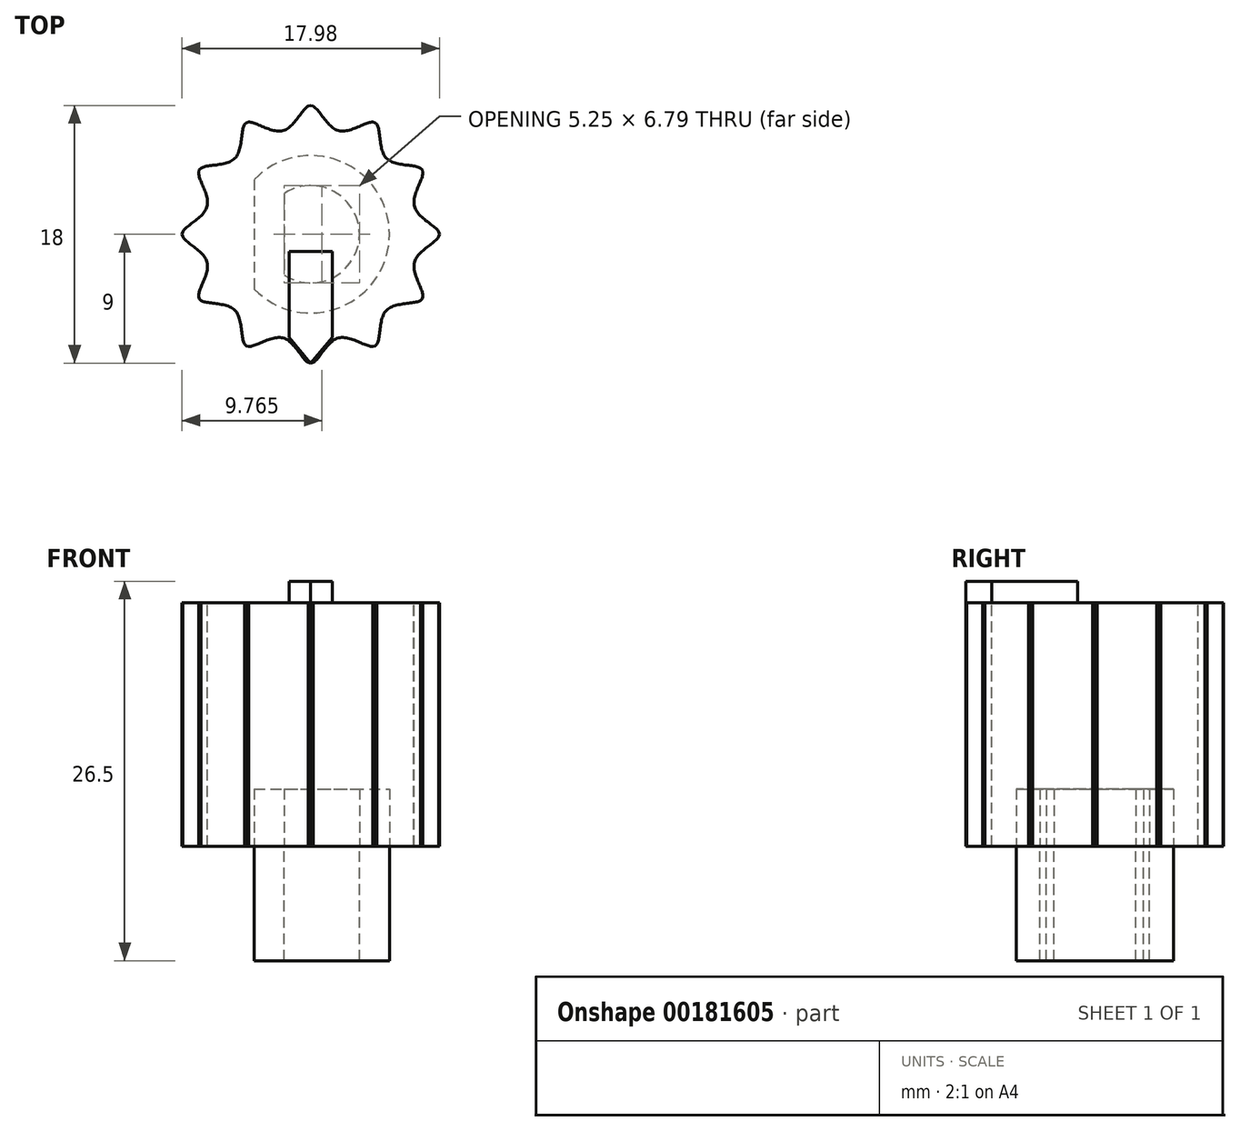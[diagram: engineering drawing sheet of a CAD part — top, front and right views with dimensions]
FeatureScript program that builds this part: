
annotation { "Feature Type Name" : "Feature", "Feature Type Description" : "" }
export const myFeature = defineFeature(function(context is Context, id is Id, definition is map)
    precondition{}
    {
        {
            var Q0;
            Q0=qCreatedBy(makeId("Top.planeOp"),FACE);
            var sketch = newSketch(context, id + "F0", { "sketchPlane" : qUnion([Q0])});
            skCircle(sketch, "E0", {"center": v(0, 0) * mm, "radius": 5.5 * mm});
            skLineSegment(sketch, "E1", {"start": v(-3.95, 3.83) * mm, "end": v(-3.95, -3.83) * mm});
            skArc(sketch, "E2", {"start": v(-1.85, 2.85) * mm, "mid": v(3.4, 0) * mm, "end": v(-1.85, -2.85) * mm});
            skLineSegment(sketch, "E3", {"start": v(-1.85, 2.85) * mm, "end": v(-1.85, -2.85) * mm});
            skLineSegment(sketch, "E4.0", {"start": v(-7.8, -4.5) * mm, "end": v(-9, 0) * mm});
            skLineSegment(sketch, "E4.1", {"start": v(-9, 0) * mm, "end": v(-7.8, 4.5) * mm});
            skLineSegment(sketch, "E4.2", {"start": v(-7.8, 4.5) * mm, "end": v(-4.5, 7.8) * mm});
            skLineSegment(sketch, "E4.3", {"start": v(-4.5, 7.8) * mm, "end": v(0, 9) * mm});
            skLineSegment(sketch, "E4.4", {"start": v(0, 9) * mm, "end": v(4.5, 7.8) * mm});
            skLineSegment(sketch, "E4.5", {"start": v(4.5, 7.8) * mm, "end": v(7.8, 4.5) * mm});
            skLineSegment(sketch, "E4.6", {"start": v(7.8, 4.5) * mm, "end": v(9, 0) * mm});
            skLineSegment(sketch, "E4.7", {"start": v(9, 0) * mm, "end": v(7.8, -4.5) * mm});
            skLineSegment(sketch, "E4.8", {"start": v(7.8, -4.5) * mm, "end": v(4.5, -7.8) * mm});
            skLineSegment(sketch, "E4.9", {"start": v(4.5, -7.8) * mm, "end": v(0, -9) * mm});
            skLineSegment(sketch, "E4.10", {"start": v(0, -9) * mm, "end": v(-4.5, -7.8) * mm});
            skLineSegment(sketch, "E4.11", {"start": v(-4.5, -7.8) * mm, "end": v(-7.8, -4.5) * mm});
            skLineSegment(sketch, "E5.0", {"start": v(1.94, 7.24) * mm, "end": v(5.3, 5.3) * mm});
            skLineSegment(sketch, "E5.1", {"start": v(5.3, 5.3) * mm, "end": v(7.24, 1.94) * mm});
            skLineSegment(sketch, "E5.2", {"start": v(7.24, 1.94) * mm, "end": v(7.24, -1.94) * mm});
            skLineSegment(sketch, "E5.3", {"start": v(7.24, -1.94) * mm, "end": v(5.3, -5.3) * mm});
            skLineSegment(sketch, "E5.4", {"start": v(5.3, -5.3) * mm, "end": v(1.94, -7.24) * mm});
            skLineSegment(sketch, "E5.5", {"start": v(1.94, -7.24) * mm, "end": v(-1.94, -7.24) * mm});
            skLineSegment(sketch, "E5.6", {"start": v(-1.94, -7.24) * mm, "end": v(-5.3, -5.3) * mm});
            skLineSegment(sketch, "E5.7", {"start": v(-5.3, -5.3) * mm, "end": v(-7.24, -1.94) * mm});
            skLineSegment(sketch, "E5.8", {"start": v(-7.24, -1.94) * mm, "end": v(-7.24, 1.94) * mm});
            skLineSegment(sketch, "E5.9", {"start": v(-7.24, 1.94) * mm, "end": v(-5.3, 5.3) * mm});
            skLineSegment(sketch, "E5.10", {"start": v(-5.3, 5.3) * mm, "end": v(-1.94, 7.24) * mm});
            skLineSegment(sketch, "E5.11", {"start": v(-1.94, 7.24) * mm, "end": v(1.94, 7.24) * mm});
            skFitSpline(sketch, "E6", {"points": [v(0, 9) * mm, v(1.94, 7.24) * mm, v(4.5, 7.8) * mm, v(5.3, 5.3) * mm, v(7.8, 4.5) * mm, v(7.24, 1.94) * mm, v(9, 0) * mm, v(7.24, -1.94) * mm, v(7.8, -4.5) * mm, v(5.3, -5.3) * mm, v(4.5, -7.8) * mm, v(1.94, -7.24) * mm, v(0, -9) * mm, v(-1.94, -7.24) * mm, v(-4.5, -7.8) * mm, v(-5.3, -5.3) * mm, v(-7.8, -4.5) * mm, v(-7.24, -1.94) * mm, v(-9, 0) * mm, v(-7.24, 1.94) * mm, v(-7.8, 4.5) * mm, v(-5.3, 5.3) * mm, v(-4.5, 7.8) * mm, v(-1.94, 7.24) * mm, v(0, 9) * mm]});
            skSolve(sketch);
        }
        {
            var Q0;
            {var subQ0=sQuery(id+"F0.wireOp",EDGE,"E3");Q0=makeQuery(id+"F0.imprint","IMPRINT",FACE,{"disambiguationData":[TD([[makeQuery(id+"F0.imprint","IMPRINT",EDGE,{"derivedFrom":subQ0}),1.0]])]});}
            var Q1;
            {var subQ0=sQuery(id+"F0.wireOp",EDGE,"E1");Q1=makeQuery(id+"F0.imprint","IMPRINT",FACE,{"disambiguationData":[TD([[makeQuery(id+"F0.imprint","IMPRINT",EDGE,{"derivedFrom":subQ0}),-1.0]])]});}
            var Q2;
            {var subQ4=sQuery(id+"F0.wireOp",EDGE,"E1");Q2=makeQuery(id+"F0.imprint","IMPRINT",FACE,{"disambiguationData":[TD([[makeQuery(id+"F0.imprint","IMPRINT",EDGE,{"derivedFrom":subQ4}),1.0]])]});}
            var Q3;
            Q3=makeQuery(id+"F0.imprint","IMPRINT",FACE,{"disambiguationData":[TD([[makeQuery(id+"F0.imprint","IMPRINT",EDGE,{"derivedFrom":sQuery(id+"F0.wireOp",EDGE,"Om1w5wkB-YJgD-hNhW-VWTO-mRfdsfstp7Lm")}),1.0]])]});
            var Q4;
            {var subQ0=sQuery(id+"F0.wireOp",EDGE,"FSIPDkNn-DrQF-lx5f-XINl-FDNYDJzQY5bG");var subQ1=sQuery(id+"F0.wireOp",EDGE,"E2");var subQ2=makeQuery(id+"F0.imprint","INTERSECT",VERTEX,{"disambiguationData":[OD(0.0)],"derivedFrom":[subQ1,subQ0]});Q4=makeQuery(id+"F0.imprint","IMPRINT",FACE,{"disambiguationData":[TD([[makeQuery(id+"F0.imprint","IMPRINT",EDGE,{"disambiguationData":[TD([[subQ2,-1.0]])],"derivedFrom":subQ1}),-1.0]])]});}
            var Q5;
            {var subQ1=sQuery(id+"F0.wireOp",EDGE,"jtoO9AOW-OG8r-op2T-0eIV-xee9z17cBor1");var subQ3=sQuery(id+"F0.wireOp",EDGE,"E0");var subQ4=makeQuery(id+"F0.imprint","INTERSECT",VERTEX,{"derivedFrom":[subQ3,subQ1]});Q5=makeQuery(id+"F0.imprint","IMPRINT",FACE,{"disambiguationData":[TD([[makeQuery(id+"F0.imprint","IMPRINT",EDGE,{"disambiguationData":[TD([[subQ4,-1.0]])],"derivedFrom":subQ3}),1.0]])]});}
            var Q6;
            {var subQ2=sQuery(id+"F0.wireOp",EDGE,"a9V57k9W-iK3Q-zI9n-wZaT-DJcMQNuYsHNN");Q6=makeQuery(id+"F0.imprint","IMPRINT",FACE,{"disambiguationData":[TD([[makeQuery(id+"F0.imprint","IMPRINT",EDGE,{"derivedFrom":subQ2}),1.0]])]});}
            var Q7;
            {var subQ0=sQuery(id+"F0.wireOp",EDGE,"11e5feca-bf29-45ad-b53b-983c72bd348e");var subQ3=sQuery(id+"F0.wireOp",EDGE,"cDvq1C5O-C3I4-aryV-n8dk-xxnMWs29t7JO");var subQ8=makeQuery(id+"F0.imprint","INTERSECT",VERTEX,{"disambiguationData":[OD(11.0)],"derivedFrom":[subQ3,subQ0]});Q7=makeQuery(id+"F0.imprint","IMPRINT",FACE,{"disambiguationData":[TD([[makeQuery(id+"F0.imprint","IMPRINT",EDGE,{"disambiguationData":[TD([[subQ8,-1.0]])],"derivedFrom":subQ3}),-1.0]])]});}
            var Q8;
            {var subQ21=sQuery(id+"F0.wireOp",EDGE,"E1");var subQ22=sQuery(id+"F0.wireOp",EDGE,"E0");var subQ23=makeQuery(id+"F0.imprint","INTERSECT",VERTEX,{"disambiguationData":[OD(0.0)],"derivedFrom":[subQ22,subQ21]});Q8=makeQuery(id+"F0.imprint","IMPRINT",FACE,{"disambiguationData":[TD([[makeQuery(id+"F0.imprint","IMPRINT",EDGE,{"disambiguationData":[TD([[subQ23,-1.0]])],"derivedFrom":subQ22}),-1.0]])]});}
            var Q9;
            {var subQ0=sQuery(id+"F0.wireOp",EDGE,"11e5feca-bf29-45ad-b53b-983c72bd348e");var subQ3=sQuery(id+"F0.wireOp",EDGE,"cDvq1C5O-C3I4-aryV-n8dk-xxnMWs29t7JO");var subQ5=makeQuery(id+"F0.imprint","INTERSECT",VERTEX,{"disambiguationData":[OD(9.0)],"derivedFrom":[subQ3,subQ0]});Q9=makeQuery(id+"F0.imprint","IMPRINT",FACE,{"disambiguationData":[TD([[makeQuery(id+"F0.imprint","IMPRINT",EDGE,{"disambiguationData":[TD([[subQ5,-1.0]])],"derivedFrom":subQ3}),-1.0]])]});}
            var Q10;
            {var subQ0=sQuery(id+"F0.wireOp",EDGE,"11e5feca-bf29-45ad-b53b-983c72bd348e");var subQ3=sQuery(id+"F0.wireOp",EDGE,"cDvq1C5O-C3I4-aryV-n8dk-xxnMWs29t7JO");var subQ5=makeQuery(id+"F0.imprint","INTERSECT",VERTEX,{"disambiguationData":[OD(7.0)],"derivedFrom":[subQ3,subQ0]});Q10=makeQuery(id+"F0.imprint","IMPRINT",FACE,{"disambiguationData":[TD([[makeQuery(id+"F0.imprint","IMPRINT",EDGE,{"disambiguationData":[TD([[subQ5,-1.0]])],"derivedFrom":subQ3}),-1.0]])]});}
            var Q11;
            {var subQ0=sQuery(id+"F0.wireOp",EDGE,"11e5feca-bf29-45ad-b53b-983c72bd348e");var subQ3=sQuery(id+"F0.wireOp",EDGE,"cDvq1C5O-C3I4-aryV-n8dk-xxnMWs29t7JO");var subQ4=makeQuery(id+"F0.imprint","INTERSECT",VERTEX,{"disambiguationData":[OD(5.0)],"derivedFrom":[subQ3,subQ0]});Q11=makeQuery(id+"F0.imprint","IMPRINT",FACE,{"disambiguationData":[TD([[makeQuery(id+"F0.imprint","IMPRINT",EDGE,{"disambiguationData":[TD([[subQ4,-1.0]])],"derivedFrom":subQ3}),-1.0]])]});}
            var Q12;
            {var subQ0=sQuery(id+"F0.wireOp",EDGE,"11e5feca-bf29-45ad-b53b-983c72bd348e");var subQ1=sQuery(id+"F0.wireOp",EDGE,"cDvq1C5O-C3I4-aryV-n8dk-xxnMWs29t7JO");var subQ2=makeQuery(id+"F0.imprint","INTERSECT",VERTEX,{"disambiguationData":[OD(3.0)],"derivedFrom":[subQ1,subQ0]});Q12=makeQuery(id+"F0.imprint","IMPRINT",FACE,{"disambiguationData":[TD([[makeQuery(id+"F0.imprint","IMPRINT",EDGE,{"disambiguationData":[TD([[subQ2,-1.0]])],"derivedFrom":subQ1}),-1.0]])]});}
            var Q13;
            {var subQ0=sQuery(id+"F0.wireOp",EDGE,"11e5feca-bf29-45ad-b53b-983c72bd348e");var subQ1=sQuery(id+"F0.wireOp",EDGE,"cDvq1C5O-C3I4-aryV-n8dk-xxnMWs29t7JO");var subQ2=makeQuery(id+"F0.imprint","INTERSECT",VERTEX,{"disambiguationData":[OD(0.0)],"derivedFrom":[subQ1,subQ0]});Q13=makeQuery(id+"F0.imprint","IMPRINT",FACE,{"disambiguationData":[TD([[makeQuery(id+"F0.imprint","IMPRINT",EDGE,{"disambiguationData":[TD([[subQ2,-1.0]])],"derivedFrom":subQ1}),-1.0]])]});}
            var Q14;
            {var subQ0=sQuery(id+"F0.wireOp",EDGE,"11e5feca-bf29-45ad-b53b-983c72bd348e");var subQ3=sQuery(id+"F0.wireOp",EDGE,"cDvq1C5O-C3I4-aryV-n8dk-xxnMWs29t7JO");var subQ4=makeQuery(id+"F0.imprint","INTERSECT",VERTEX,{"disambiguationData":[OD(1.0)],"derivedFrom":[subQ3,subQ0]});Q14=makeQuery(id+"F0.imprint","IMPRINT",FACE,{"disambiguationData":[TD([[makeQuery(id+"F0.imprint","IMPRINT",EDGE,{"disambiguationData":[TD([[subQ4,1.0]])],"derivedFrom":subQ3}),-1.0]])]});}
            var Q15;
            {var subQ0=sQuery(id+"F0.wireOp",EDGE,"11e5feca-bf29-45ad-b53b-983c72bd348e");var subQ3=sQuery(id+"F0.wireOp",EDGE,"cDvq1C5O-C3I4-aryV-n8dk-xxnMWs29t7JO");var subQ5=makeQuery(id+"F0.imprint","INTERSECT",VERTEX,{"disambiguationData":[OD(19.0)],"derivedFrom":[subQ3,subQ0]});Q15=makeQuery(id+"F0.imprint","IMPRINT",FACE,{"disambiguationData":[TD([[makeQuery(id+"F0.imprint","IMPRINT",EDGE,{"disambiguationData":[TD([[subQ5,-1.0]])],"derivedFrom":subQ3}),-1.0]])]});}
            var Q16;
            {var subQ0=sQuery(id+"F0.wireOp",EDGE,"11e5feca-bf29-45ad-b53b-983c72bd348e");var subQ3=sQuery(id+"F0.wireOp",EDGE,"cDvq1C5O-C3I4-aryV-n8dk-xxnMWs29t7JO");var subQ5=makeQuery(id+"F0.imprint","INTERSECT",VERTEX,{"disambiguationData":[OD(15.0)],"derivedFrom":[subQ3,subQ0]});Q16=makeQuery(id+"F0.imprint","IMPRINT",FACE,{"disambiguationData":[TD([[makeQuery(id+"F0.imprint","IMPRINT",EDGE,{"disambiguationData":[TD([[subQ5,-1.0]])],"derivedFrom":subQ3}),-1.0]])]});}
            var Q17;
            {var subQ0=sQuery(id+"F0.wireOp",EDGE,"11e5feca-bf29-45ad-b53b-983c72bd348e");var subQ3=sQuery(id+"F0.wireOp",EDGE,"cDvq1C5O-C3I4-aryV-n8dk-xxnMWs29t7JO");var subQ8=makeQuery(id+"F0.imprint","INTERSECT",VERTEX,{"disambiguationData":[OD(13.0)],"derivedFrom":[subQ3,subQ0]});Q17=makeQuery(id+"F0.imprint","IMPRINT",FACE,{"disambiguationData":[TD([[makeQuery(id+"F0.imprint","IMPRINT",EDGE,{"disambiguationData":[TD([[subQ8,-1.0]])],"derivedFrom":subQ3}),-1.0]])]});}
            var Q18;
            {var subQ0=sQuery(id+"F0.wireOp",EDGE,"11e5feca-bf29-45ad-b53b-983c72bd348e");var subQ10=sQuery(id+"F0.wireOp",EDGE,"cDvq1C5O-C3I4-aryV-n8dk-xxnMWs29t7JO");var subQ11=makeQuery(id+"F0.imprint","INTERSECT",VERTEX,{"disambiguationData":[OD(17.0)],"derivedFrom":[subQ10,subQ0]});Q18=makeQuery(id+"F0.imprint","IMPRINT",FACE,{"disambiguationData":[TD([[makeQuery(id+"F0.imprint","IMPRINT",EDGE,{"disambiguationData":[TD([[subQ11,-1.0]])],"derivedFrom":subQ10}),-1.0]])]});}
            var Q19;
            {var subQ1=sQuery(id+"F0.wireOp",EDGE,"1e3f36e5-b42d-4e4f-be57-9027b425eaef.9");Q19=makeQuery(id+"F0.imprint","IMPRINT",FACE,{"disambiguationData":[TD([[makeQuery(id+"F0.imprint","IMPRINT",EDGE,{"derivedFrom":subQ1}),1.0]])]});}
            var Q20;
            {var subQ1=sQuery(id+"F0.wireOp",EDGE,"1e3f36e5-b42d-4e4f-be57-9027b425eaef.10");Q20=makeQuery(id+"F0.imprint","IMPRINT",FACE,{"disambiguationData":[TD([[makeQuery(id+"F0.imprint","IMPRINT",EDGE,{"derivedFrom":subQ1}),1.0]])]});}
            var Q21;
            {var subQ0=sQuery(id+"F0.wireOp",EDGE,"1e3f36e5-b42d-4e4f-be57-9027b425eaef.11");Q21=makeQuery(id+"F0.imprint","IMPRINT",FACE,{"disambiguationData":[TD([[makeQuery(id+"F0.imprint","IMPRINT",EDGE,{"derivedFrom":subQ0}),1.0]])]});}
            var Q22;
            {var subQ1=sQuery(id+"F0.wireOp",EDGE,"1e3f36e5-b42d-4e4f-be57-9027b425eaef.0");Q22=makeQuery(id+"F0.imprint","IMPRINT",FACE,{"disambiguationData":[TD([[makeQuery(id+"F0.imprint","IMPRINT",EDGE,{"derivedFrom":subQ1}),1.0]])]});}
            var Q23;
            {var subQ1=sQuery(id+"F0.wireOp",EDGE,"1e3f36e5-b42d-4e4f-be57-9027b425eaef.1");Q23=makeQuery(id+"F0.imprint","IMPRINT",FACE,{"disambiguationData":[TD([[makeQuery(id+"F0.imprint","IMPRINT",EDGE,{"derivedFrom":subQ1}),1.0]])]});}
            var Q24;
            {var subQ1=sQuery(id+"F0.wireOp",EDGE,"1e3f36e5-b42d-4e4f-be57-9027b425eaef.2");Q24=makeQuery(id+"F0.imprint","IMPRINT",FACE,{"disambiguationData":[TD([[makeQuery(id+"F0.imprint","IMPRINT",EDGE,{"derivedFrom":subQ1}),1.0]])]});}
            var Q25;
            {var subQ1=sQuery(id+"F0.wireOp",EDGE,"1e3f36e5-b42d-4e4f-be57-9027b425eaef.3");Q25=makeQuery(id+"F0.imprint","IMPRINT",FACE,{"disambiguationData":[TD([[makeQuery(id+"F0.imprint","IMPRINT",EDGE,{"derivedFrom":subQ1}),1.0]])]});}
            var Q26;
            {var subQ0=sQuery(id+"F0.wireOp",EDGE,"1e3f36e5-b42d-4e4f-be57-9027b425eaef.4");Q26=makeQuery(id+"F0.imprint","IMPRINT",FACE,{"disambiguationData":[TD([[makeQuery(id+"F0.imprint","IMPRINT",EDGE,{"derivedFrom":subQ0}),1.0]])]});}
            var Q27;
            {var subQ1=sQuery(id+"F0.wireOp",EDGE,"1e3f36e5-b42d-4e4f-be57-9027b425eaef.5");Q27=makeQuery(id+"F0.imprint","IMPRINT",FACE,{"disambiguationData":[TD([[makeQuery(id+"F0.imprint","IMPRINT",EDGE,{"derivedFrom":subQ1}),1.0]])]});}
            var Q28;
            {var subQ1=sQuery(id+"F0.wireOp",EDGE,"1e3f36e5-b42d-4e4f-be57-9027b425eaef.6");Q28=makeQuery(id+"F0.imprint","IMPRINT",FACE,{"disambiguationData":[TD([[makeQuery(id+"F0.imprint","IMPRINT",EDGE,{"derivedFrom":subQ1}),1.0]])]});}
            var Q29;
            {var subQ1=sQuery(id+"F0.wireOp",EDGE,"1e3f36e5-b42d-4e4f-be57-9027b425eaef.7");Q29=makeQuery(id+"F0.imprint","IMPRINT",FACE,{"disambiguationData":[TD([[makeQuery(id+"F0.imprint","IMPRINT",EDGE,{"derivedFrom":subQ1}),1.0]])]});}
            var Q30;
            {var subQ5=sQuery(id+"F0.wireOp",EDGE,"1e3f36e5-b42d-4e4f-be57-9027b425eaef.8");Q30=makeQuery(id+"F0.imprint","IMPRINT",FACE,{"disambiguationData":[TD([[makeQuery(id+"F0.imprint","IMPRINT",EDGE,{"derivedFrom":subQ5}),1.0]])]});}
            var Q31;
            {var subQ1=sQuery(id+"F0.wireOp",EDGE,"E5.10");Q31=makeQuery(id+"F0.imprint","IMPRINT",FACE,{"disambiguationData":[TD([[makeQuery(id+"F0.imprint","IMPRINT",EDGE,{"derivedFrom":subQ1}),1.0]])]});}
            var Q32;
            {var subQ0=sQuery(id+"F0.wireOp",EDGE,"E5.11");Q32=makeQuery(id+"F0.imprint","IMPRINT",FACE,{"disambiguationData":[TD([[makeQuery(id+"F0.imprint","IMPRINT",EDGE,{"derivedFrom":subQ0}),1.0]])]});}
            var Q33;
            {var subQ1=sQuery(id+"F0.wireOp",EDGE,"E5.0");Q33=makeQuery(id+"F0.imprint","IMPRINT",FACE,{"disambiguationData":[TD([[makeQuery(id+"F0.imprint","IMPRINT",EDGE,{"derivedFrom":subQ1}),1.0]])]});}
            var Q34;
            {var subQ1=sQuery(id+"F0.wireOp",EDGE,"E5.1");Q34=makeQuery(id+"F0.imprint","IMPRINT",FACE,{"disambiguationData":[TD([[makeQuery(id+"F0.imprint","IMPRINT",EDGE,{"derivedFrom":subQ1}),1.0]])]});}
            var Q35;
            {var subQ1=sQuery(id+"F0.wireOp",EDGE,"E5.2");Q35=makeQuery(id+"F0.imprint","IMPRINT",FACE,{"disambiguationData":[TD([[makeQuery(id+"F0.imprint","IMPRINT",EDGE,{"derivedFrom":subQ1}),1.0]])]});}
            var Q36;
            {var subQ1=sQuery(id+"F0.wireOp",EDGE,"E5.3");Q36=makeQuery(id+"F0.imprint","IMPRINT",FACE,{"disambiguationData":[TD([[makeQuery(id+"F0.imprint","IMPRINT",EDGE,{"derivedFrom":subQ1}),1.0]])]});}
            var Q37;
            {var subQ0=sQuery(id+"F0.wireOp",EDGE,"E5.4");Q37=makeQuery(id+"F0.imprint","IMPRINT",FACE,{"disambiguationData":[TD([[makeQuery(id+"F0.imprint","IMPRINT",EDGE,{"derivedFrom":subQ0}),1.0]])]});}
            var Q38;
            {var subQ1=sQuery(id+"F0.wireOp",EDGE,"E5.5");Q38=makeQuery(id+"F0.imprint","IMPRINT",FACE,{"disambiguationData":[TD([[makeQuery(id+"F0.imprint","IMPRINT",EDGE,{"derivedFrom":subQ1}),1.0]])]});}
            var Q39;
            {var subQ1=sQuery(id+"F0.wireOp",EDGE,"E5.6");Q39=makeQuery(id+"F0.imprint","IMPRINT",FACE,{"disambiguationData":[TD([[makeQuery(id+"F0.imprint","IMPRINT",EDGE,{"derivedFrom":subQ1}),1.0]])]});}
            var Q40;
            {var subQ1=sQuery(id+"F0.wireOp",EDGE,"E5.7");Q40=makeQuery(id+"F0.imprint","IMPRINT",FACE,{"disambiguationData":[TD([[makeQuery(id+"F0.imprint","IMPRINT",EDGE,{"derivedFrom":subQ1}),1.0]])]});}
            var Q41;
            {var subQ5=sQuery(id+"F0.wireOp",EDGE,"E5.8");Q41=makeQuery(id+"F0.imprint","IMPRINT",FACE,{"disambiguationData":[TD([[makeQuery(id+"F0.imprint","IMPRINT",EDGE,{"derivedFrom":subQ5}),1.0]])]});}
            var Q42;
            {var subQ1=sQuery(id+"F0.wireOp",EDGE,"E5.9");Q42=makeQuery(id+"F0.imprint","IMPRINT",FACE,{"disambiguationData":[TD([[makeQuery(id+"F0.imprint","IMPRINT",EDGE,{"derivedFrom":subQ1}),1.0]])]});}
            extrude(context, id + "F1", {"entities" : qUnion([Q0, Q1, Q2, Q3, Q4, Q5, Q6, Q7, Q8, Q9, Q10, Q11, Q12, Q13, Q14, Q15, Q16, Q17, Q18, Q19, Q20, Q21, Q22, Q23, Q24, Q25, Q26, Q27, Q28, Q29, Q30, Q31, Q32, Q33, Q34, Q35, Q36, Q37, Q38, Q39, Q40, Q41, Q42]), "depth" : 17 * mm});
        }
        {
            var Q0;
            {var subQ0=sQuery(id+"F0.wireOp",EDGE,"E1");Q0=makeQuery(id+"F0.imprint","IMPRINT",FACE,{"disambiguationData":[TD([[makeQuery(id+"F0.imprint","IMPRINT",EDGE,{"derivedFrom":subQ0}),1.0]])]});}
            var Q1;
            {var subQ5=sQuery(id+"F0.wireOp",EDGE,"FSIPDkNn-DrQF-lx5f-XINl-FDNYDJzQY5bG");Q1=makeQuery(id+"F0.imprint","IMPRINT",FACE,{"disambiguationData":[TD([[makeQuery(id+"F0.imprint","IMPRINT",EDGE,{"derivedFrom":subQ5}),-1.0]])]});}
            extrude(context, id + "F2", {"entities" : qUnion([Q0, Q1]), "operationType" : NewBodyOperationType.ADD, "oppositeDirection" : true, "depth" : 8 * mm});
        }
        {
            var Q0;
            Q0=makeQuery(id+"F0.imprint","IMPRINT",FACE,{"disambiguationData":[TD([[makeQuery(id+"F0.imprint","IMPRINT",EDGE,{"derivedFrom":sQuery(id+"F0.wireOp",EDGE,"E2")}),-1.0]])]});
            extrude(context, id + "F3", {"entities" : qUnion([Q0]), "operationType" : NewBodyOperationType.REMOVE, "depth" : 4 * mm});
        }
        {
            var Q0;
            Q0=makeQuery(id+"F1.opExtrude","CAP_FACE",FACE,{"disambiguationData":[OSD([sQuery(id+"F0.wireOp",EDGE,"E4.0"),sQuery(id+"F0.wireOp",EDGE,"E4.1"),sQuery(id+"F0.wireOp",EDGE,"E4.2"),sQuery(id+"F0.wireOp",EDGE,"E4.3"),sQuery(id+"F0.wireOp",EDGE,"E4.4"),sQuery(id+"F0.wireOp",EDGE,"E4.5"),sQuery(id+"F0.wireOp",EDGE,"E4.6"),sQuery(id+"F0.wireOp",EDGE,"E4.7"),sQuery(id+"F0.wireOp",EDGE,"E4.8"),sQuery(id+"F0.wireOp",EDGE,"E4.9"),sQuery(id+"F0.wireOp",EDGE,"E4.10"),sQuery(id+"F0.wireOp",EDGE,"E4.11")])],"isStart":false});
            var sketch = newSketch(context, id + "F4", { "sketchPlane" : qUnion([Q0])});
            skLineSegment(sketch, "E7", {"start": v(-1.5, -7.21) * mm, "end": v(-1.5, -1.21) * mm});
            skLineSegment(sketch, "E8", {"start": v(1.5, -7.21) * mm, "end": v(1.5, -1.21) * mm});
            skLineSegment(sketch, "E9", {"start": v(1.5, -1.21) * mm, "end": v(-1.5, -1.21) * mm});
            skLineSegment(sketch, "E10", {"start": v(0, -9) * mm, "end": v(1.5, -7.21) * mm});
            skLineSegment(sketch, "E11", {"start": v(0, -9) * mm, "end": v(-1.5, -7.21) * mm});
            skSolve(sketch);
        }
        {
            var Q0;
            Q0=makeQuery(id+"F4.imprint","IMPRINT",FACE,{"disambiguationData":[TD([[makeQuery(id+"F4.imprint","IMPRINT",EDGE,{"derivedFrom":sQuery(id+"F4.wireOp",EDGE,"E7")}),-1.0]])]});
            extrude(context, id + "F5", {"entities" : qUnion([Q0]), "operationType" : NewBodyOperationType.ADD, "depth" : 1.5 * mm});
        }
    });
